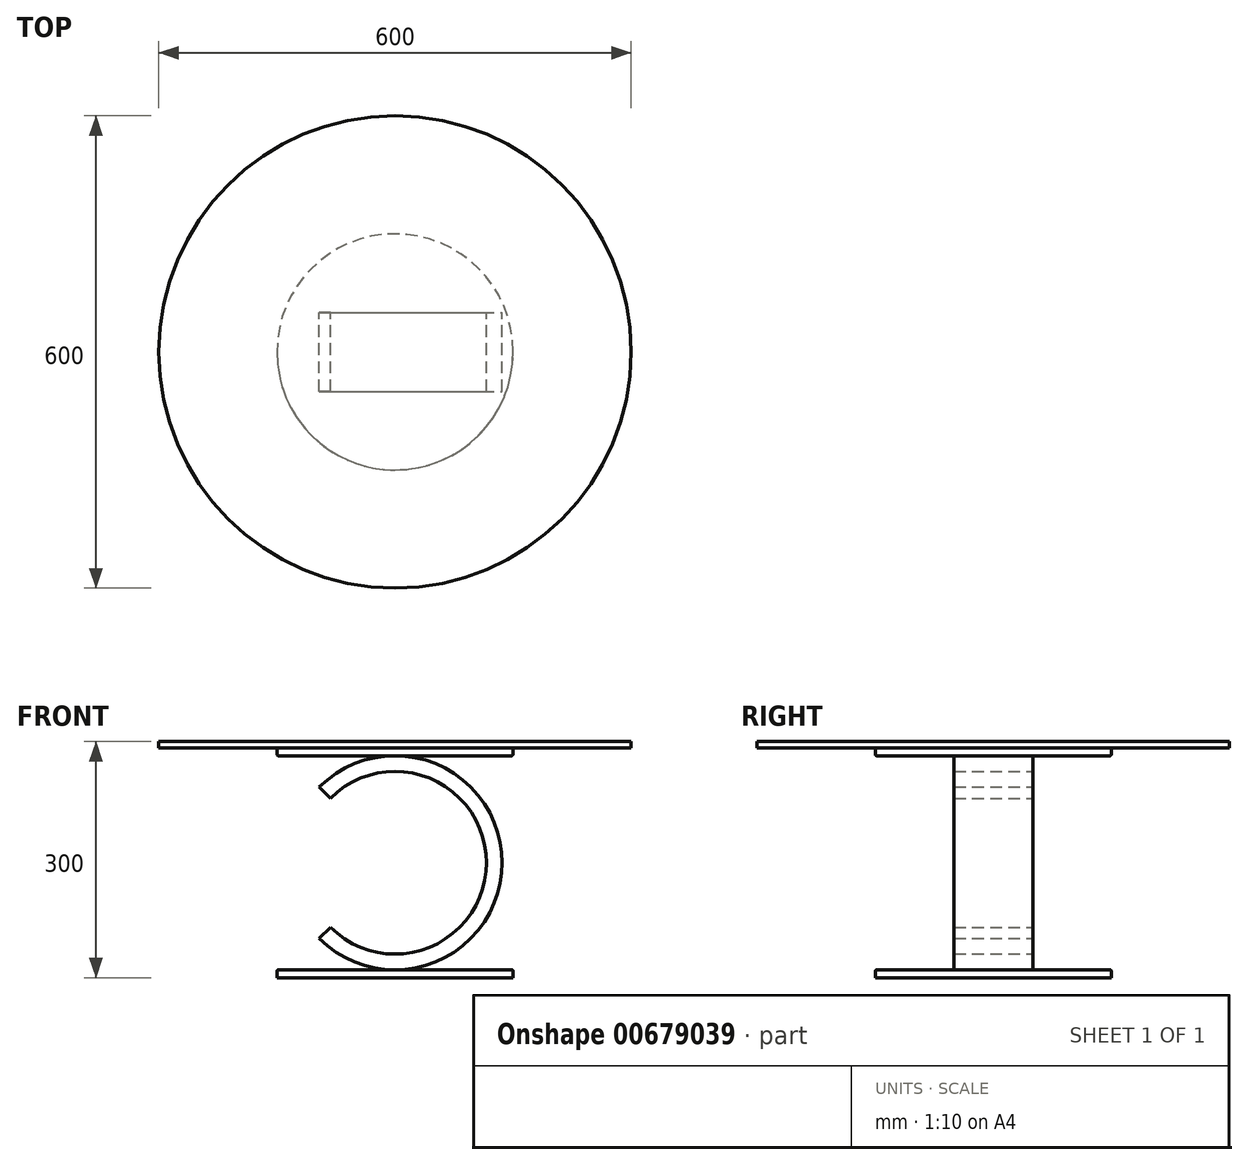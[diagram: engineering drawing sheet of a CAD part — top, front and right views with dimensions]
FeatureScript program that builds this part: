
annotation { "Feature Type Name" : "Feature", "Feature Type Description" : "" }
export const myFeature = defineFeature(function(context is Context, id is Id, definition is map)
    precondition{}
    {
        {
            var Q0;
            Q0=qCreatedBy(makeId("Front.planeOp"),FACE);
            var sketch = newSketch(context, id + "F0", { "sketchPlane" : qUnion([Q0])});
            skLineSegment(sketch, "E0", {"start": v(0, 0) * mm, "end": v(150, 0) * mm});
            skLineSegment(sketch, "E1", {"start": v(150, 0) * mm, "end": v(150, 10) * mm});
            skLineSegment(sketch, "E2", {"start": v(150, 10) * mm, "end": v(-150, 10) * mm});
            skLineSegment(sketch, "E3", {"start": v(-150, 10) * mm, "end": v(-150, 0) * mm});
            skLineSegment(sketch, "E4", {"start": v(-150, 0) * mm, "end": v(0, 0) * mm});
            skArc(sketch, "E5", {"start": v(0, 10) * mm, "mid": v(136, 146) * mm, "end": v(0, 282) * mm});
            skPoint(sketch, "E5.endSnap0", {"position": v(0, 10) * mm});
            skLineSegment(sketch, "E6", {"start": v(0, 282) * mm, "end": v(0, 262) * mm});
            skLineSegment(sketch, "E7", {"start": v(0, 10) * mm, "end": v(0, 30) * mm});
            skArc(sketch, "E8", {"start": v(0, 30) * mm, "mid": v(116, 146) * mm, "end": v(0, 262) * mm});
            skLineSegment(sketch, "E9", {"start": v(0, 282) * mm, "end": v(150, 282) * mm});
            skLineSegment(sketch, "E10", {"start": v(150, 282) * mm, "end": v(150, 292) * mm});
            skLineSegment(sketch, "E11", {"start": v(150, 292) * mm, "end": v(-150, 292) * mm});
            skLineSegment(sketch, "E12", {"start": v(-150, 292) * mm, "end": v(-150, 282) * mm});
            skLineSegment(sketch, "E13", {"start": v(-150, 282) * mm, "end": v(0, 282) * mm});
            skPoint(sketch, "E14.oppositeSnap0", {"position": v(0, 292) * mm});
            skLineSegment(sketch, "E15", {"start": v(-150, 292) * mm, "end": v(-300, 292) * mm});
            skLineSegment(sketch, "E16", {"start": v(-300, 292) * mm, "end": v(-300, 300) * mm});
            skLineSegment(sketch, "E17", {"start": v(-300, 300) * mm, "end": v(300, 300) * mm});
            skLineSegment(sketch, "E18", {"start": v(300, 300) * mm, "end": v(300, 292) * mm});
            skLineSegment(sketch, "E19", {"start": v(300, 292) * mm, "end": v(150, 292) * mm});
            skArc(sketch, "E20", {"start": v(0, 282) * mm, "mid": v(-52.04, 271.65) * mm, "end": v(-96.17, 242.17) * mm});
            skArc(sketch, "E21", {"start": v(0, 262) * mm, "mid": v(-44.4, 253.17) * mm, "end": v(-82.02, 228.02) * mm});
            skArc(sketch, "E22", {"start": v(-82.02, 63.98) * mm, "mid": v(-44.4, 38.83) * mm, "end": v(0, 30) * mm});
            skArc(sketch, "E23", {"start": v(-96.17, 49.83) * mm, "mid": v(-52.04, 20.35) * mm, "end": v(0, 10) * mm});
            skLineSegment(sketch, "E24", {"start": v(0, 146) * mm, "end": v(-96.17, 242.17) * mm});
            skLineSegment(sketch, "E25", {"start": v(0, 146) * mm, "end": v(-96.17, 49.83) * mm});
            skLineSegment(sketch, "E26", {"start": v(-96.17, 242.17) * mm, "end": v(-96.17, 282) * mm, "construction": true});
            skLineSegment(sketch, "E27", {"start": v(-96.17, 49.83) * mm, "end": v(-96.17, 10) * mm, "construction": true});
            skLineSegment(sketch, "E28", {"start": v(-96.17, 242.17) * mm, "end": v(-96.17, 49.83) * mm, "construction": true});
            skSolve(sketch);
        }
        {
            var Q0;
            Q0=makeQuery(id+"F0.imprint","IMPRINT",FACE,{"disambiguationData":[TD([[makeQuery(id+"F0.imprint","IMPRINT",EDGE,{"derivedFrom":sQuery(id+"F0.wireOp",EDGE,"E11")}),-1.0]])]});
            extrude(context, id + "F1", {"entities" : qUnion([Q0]), "depth" : 300 * mm, "offsetDistance" : 25 * mm, "hasSecondDirection" : true, "secondDirectionOppositeDirection" : true, "secondDirectionDepth" : 300 * mm});
        }
        {
            var Q0;
            Q0=makeQuery(id+"F0.imprint","IMPRINT",FACE,{"disambiguationData":[TD([[makeQuery(id+"F0.imprint","IMPRINT",EDGE,{"derivedFrom":sQuery(id+"F0.wireOp",EDGE,"E9")}),1.0]])]});
            var Q1;
            Q1=makeQuery(id+"F0.imprint","IMPRINT",FACE,{"disambiguationData":[TD([[makeQuery(id+"F0.imprint","IMPRINT",EDGE,{"derivedFrom":sQuery(id+"F0.wireOp",EDGE,"E0")}),1.0]])]});
            extrude(context, id + "F2", {"entities" : qUnion([Q0, Q1]), "depth" : 150 * mm, "offsetDistance" : 25 * mm, "hasSecondDirection" : true, "secondDirectionOppositeDirection" : true, "secondDirectionDepth" : 150 * mm});
        }
        {
            var Q0;
            Q0=makeQuery(id+"F0.imprint","IMPRINT",FACE,{"disambiguationData":[TD([[makeQuery(id+"F0.imprint","IMPRINT",EDGE,{"derivedFrom":sQuery(id+"F0.wireOp",EDGE,"E5")}),1.0]])]});
            var Q1;
            Q1=makeQuery(id+"F0.imprint","IMPRINT",FACE,{"disambiguationData":[TD([[makeQuery(id+"F0.imprint","IMPRINT",EDGE,{"derivedFrom":sQuery(id+"F0.wireOp",EDGE,"E6")}),-1.0]])]});
            var Q2;
            Q2=makeQuery(id+"F0.imprint","IMPRINT",FACE,{"disambiguationData":[TD([[makeQuery(id+"F0.imprint","IMPRINT",EDGE,{"derivedFrom":sQuery(id+"F0.wireOp",EDGE,"E7")}),1.0]])]});
            extrude(context, id + "F3", {"entities" : qUnion([Q0, Q1, Q2]), "depth" : 50 * mm, "offsetDistance" : 25 * mm, "hasSecondDirection" : true, "secondDirectionOppositeDirection" : true, "secondDirectionDepth" : 50 * mm});
        }
        {
            var Q0;
            Q0=makeQuery(id+"F1.opExtrude","CAP_EDGE",EDGE,{"disambiguationData":[OSD([sQuery(id+"F0.wireOp",EDGE,"E16")])],"isStart":true});
            var Q1;
            Q1=makeQuery(id+"F1.opExtrude","CAP_EDGE",EDGE,{"disambiguationData":[OSD([sQuery(id+"F0.wireOp",EDGE,"E16")])],"isStart":false});
            var Q2;
            Q2=makeQuery(id+"F1.opExtrude","CAP_EDGE",EDGE,{"disambiguationData":[OSD([sQuery(id+"F0.wireOp",EDGE,"E18")])],"isStart":true});
            var Q3;
            Q3=makeQuery(id+"F1.opExtrude","CAP_EDGE",EDGE,{"disambiguationData":[OSD([sQuery(id+"F0.wireOp",EDGE,"E18")])],"isStart":false});
            fillet(context, id + "F4", {"entities" : qUnion([Q0, Q1, Q2, Q3]), "radius" : 300 * mm, "tangentPropagation" : true, "allowEdgeOverflow" : false});
        }
        {
            var Q0;
            Q0=makeQuery(id+"F2.opExtrude","CAP_EDGE",EDGE,{"disambiguationData":[OSD([sQuery(id+"F0.wireOp",EDGE,"E10")])],"isStart":false});
            var Q1;
            Q1=makeQuery(id+"F2.opExtrude","CAP_EDGE",EDGE,{"disambiguationData":[OSD([sQuery(id+"F0.wireOp",EDGE,"E10")])],"isStart":true});
            var Q2;
            Q2=makeQuery(id+"F2.opExtrude","CAP_EDGE",EDGE,{"disambiguationData":[OSD([sQuery(id+"F0.wireOp",EDGE,"E1")])],"isStart":false});
            var Q3;
            Q3=makeQuery(id+"F2.opExtrude","CAP_EDGE",EDGE,{"disambiguationData":[OSD([sQuery(id+"F0.wireOp",EDGE,"E1")])],"isStart":true});
            var Q4;
            Q4=makeQuery(id+"F2.opExtrude","CAP_EDGE",EDGE,{"disambiguationData":[OSD([sQuery(id+"F0.wireOp",EDGE,"E12")])],"isStart":true});
            var Q5;
            Q5=makeQuery(id+"F2.opExtrude","CAP_EDGE",EDGE,{"disambiguationData":[OSD([sQuery(id+"F0.wireOp",EDGE,"E12")])],"isStart":false});
            var Q6;
            Q6=makeQuery(id+"F2.opExtrude","CAP_EDGE",EDGE,{"disambiguationData":[OSD([sQuery(id+"F0.wireOp",EDGE,"E3")])],"isStart":false});
            var Q7;
            Q7=makeQuery(id+"F2.opExtrude","CAP_EDGE",EDGE,{"disambiguationData":[OSD([sQuery(id+"F0.wireOp",EDGE,"E3")])],"isStart":true});
            fillet(context, id + "F5", {"entities" : qUnion([Q0, Q1, Q2, Q3, Q4, Q5, Q6, Q7]), "radius" : 150 * mm, "tangentPropagation" : true, "allowEdgeOverflow" : false});
        }
        {
            var Q0;
            Q0=makeQuery(id+"F2.opExtrude","SWEPT_FACE",FACE,{"disambiguationData":[OSD([sQuery(id+"F0.wireOp",EDGE,"E9"),sQuery(id+"F0.wireOp",EDGE,"E13")])]});
            var Q1;
            Q1=makeQuery(id+"F2.opExtrude","SWEPT_FACE",FACE,{"disambiguationData":[OSD([sQuery(id+"F0.wireOp",EDGE,"E2")])]});
            fillet(context, id + "F6", {"entities" : qUnion([Q0, Q1]), "radius" : 2 * mm, "tangentPropagation" : true, "allowEdgeOverflow" : false});
        }
    });
